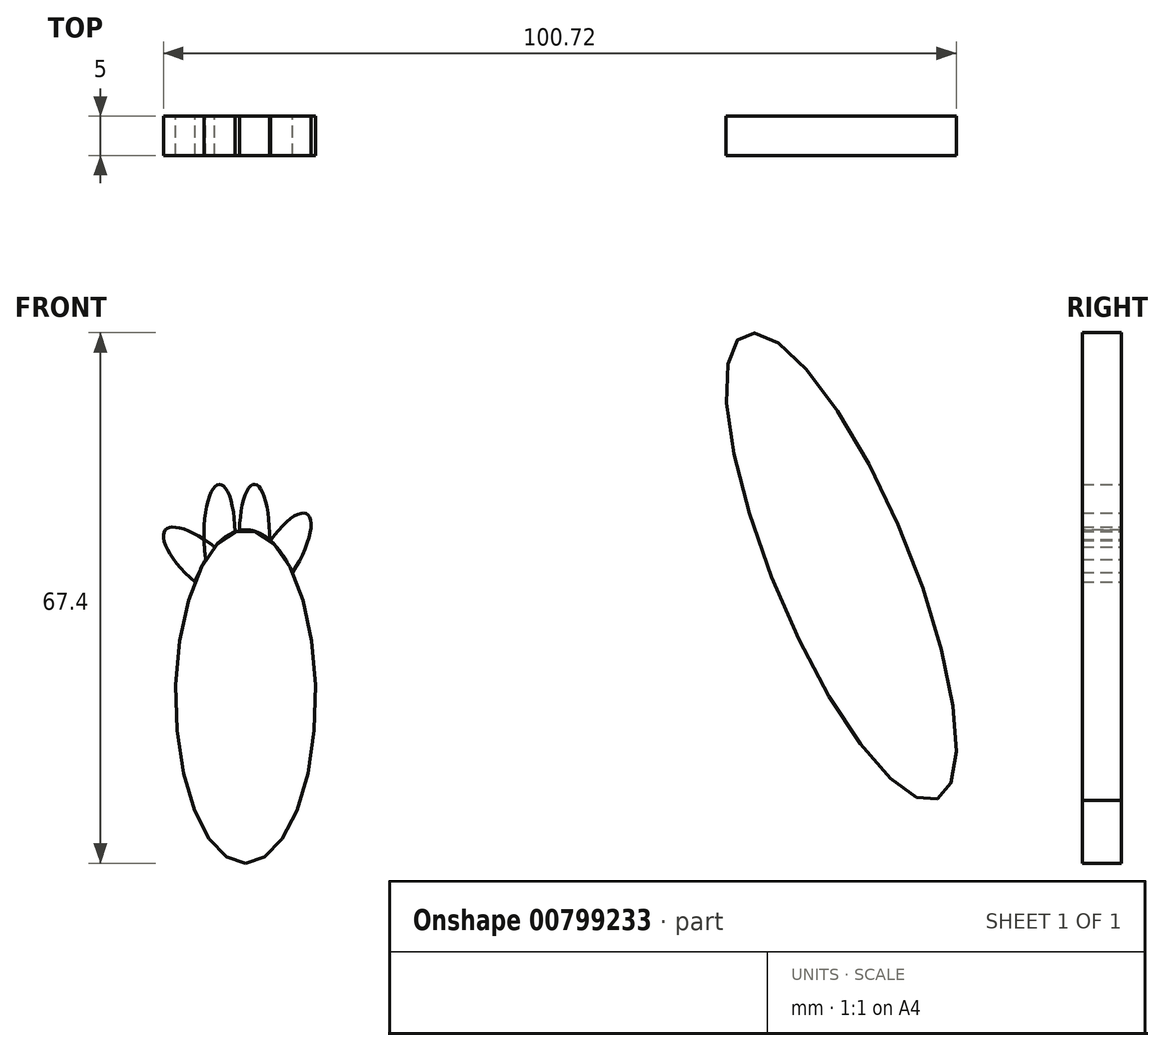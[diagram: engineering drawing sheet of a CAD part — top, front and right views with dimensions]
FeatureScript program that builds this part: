
annotation { "Feature Type Name" : "Feature", "Feature Type Description" : "" }
export const myFeature = defineFeature(function(context is Context, id is Id, definition is map)
    precondition{}
    {
        {
            var Q0;
            Q0=qCreatedBy(makeId("Front.planeOp"),FACE);
            var sketch = newSketch(context, id + "F0", { "sketchPlane" : qUnion([Q0])});
            skEllipse(sketch, "E0", {"center": v(-51.24, 0) * mm, "majorRadius": 21.18 * mm, "minorRadius": 8.9 * mm, "majorAxis": v(0, -1)});
            skSolve(sketch);
        }
        {
            var Q0;
            Q0=qCreatedBy(makeId("Front.planeOp"),FACE);
            var sketch = newSketch(context, id + "F1", { "sketchPlane" : qUnion([Q0])});
            skEllipse(sketch, "E1", {"center": v(24.4, 16.53) * mm, "majorRadius": 31.93 * mm, "minorRadius": 8.71 * mm, "majorAxis": v(0.38, -0.92)});
            skSolve(sketch);
        }
        {
            var Q0;
            Q0=makeQuery(id+"F0.imprint","IMPRINT",FACE,{"disambiguationData":[TD([[makeQuery(id+"F0.imprint","IMPRINT",EDGE,{"derivedFrom":sQuery(id+"F0.wireOp",EDGE,"E0")}),1.0]])]});
            var sketch = newSketch(context, id + "F2", { "sketchPlane" : qUnion([Q0])});
            skEllipse(sketch, "E2", {"center": v(-54.57, 20.52) * mm, "majorRadius": 6.43 * mm, "minorRadius": 1.98 * mm, "majorAxis": v(0, -1)});
            skEllipse(sketch, "E3", {"center": v(-50.13, 20.52) * mm, "majorRadius": 6.43 * mm, "minorRadius": 1.92 * mm, "majorAxis": v(0, -1)});
            skEllipse(sketch, "E4", {"center": v(-46.8, 17.64) * mm, "majorRadius": 6.47 * mm, "minorRadius": 2.27 * mm, "majorAxis": v(-0.51, -0.86)});
            skEllipse(sketch, "E5", {"center": v(-56.12, 16.51) * mm, "majorRadius": 7.07 * mm, "minorRadius": 2.5 * mm, "majorAxis": v(0.75, -0.66)});
            skSolve(sketch);
        }
        {
            var Q0;
            Q0=makeQuery(id+"F1.imprint","IMPRINT",FACE,{"disambiguationData":[TD([[makeQuery(id+"F1.imprint","IMPRINT",EDGE,{"derivedFrom":sQuery(id+"F1.wireOp",EDGE,"E1")}),1.0]])]});
            var Q1;
            Q1=makeQuery(id+"F0.imprint","IMPRINT",FACE,{"disambiguationData":[TD([[makeQuery(id+"F0.imprint","IMPRINT",EDGE,{"derivedFrom":sQuery(id+"F0.wireOp",EDGE,"E0")}),1.0]])]});
            var Q2;
            {var subQ0=sQuery(id+"F2.wireOp",EDGE,"E5");var subQ1=sQuery(id+"F2.wireOp",EDGE,"E2");var subQ2=makeQuery(id+"F2.imprint","INTERSECT",VERTEX,{"disambiguationData":[OD(0.0)],"derivedFrom":[subQ1,subQ0]});Q2=makeQuery(id+"F2.imprint","IMPRINT",FACE,{"disambiguationData":[TD([[makeQuery(id+"F2.imprint","IMPRINT",EDGE,{"disambiguationData":[TD([[subQ2,-1.0]])],"derivedFrom":subQ1}),-1.0]])]});}
            var Q3;
            {var subQ0=sQuery(id+"F2.wireOp",EDGE,"E5");var subQ1=sQuery(id+"F2.wireOp",EDGE,"E2");var subQ2=makeQuery(id+"F2.imprint","INTERSECT",VERTEX,{"disambiguationData":[OD(0.0)],"derivedFrom":[subQ1,subQ0]});Q3=makeQuery(id+"F2.imprint","IMPRINT",FACE,{"disambiguationData":[TD([[makeQuery(id+"F2.imprint","IMPRINT",EDGE,{"disambiguationData":[TD([[subQ2,1.0]])],"derivedFrom":subQ1}),1.0]])]});}
            var Q4;
            {var subQ0=sQuery(id+"F2.wireOp",EDGE,"E3");var subQ1=makeQuery(id+"F0.imprint","IMPRINT",EDGE,{"derivedFrom":sQuery(id+"F0.wireOp",EDGE,"E0")});var subQ2=makeQuery(id+"F2.imprint","INTERSECT",VERTEX,{"disambiguationData":[OD(0.0)],"derivedFrom":[subQ1,subQ0]});Q4=makeQuery(id+"F2.imprint","IMPRINT",FACE,{"disambiguationData":[TD([[makeQuery(id+"F2.imprint","IMPRINT",EDGE,{"disambiguationData":[TD([[subQ2,-1.0]])],"derivedFrom":subQ0}),1.0]])]});}
            var Q5;
            {var subQ0=sQuery(id+"F2.wireOp",EDGE,"E4");var subQ1=makeQuery(id+"F0.imprint","IMPRINT",EDGE,{"derivedFrom":sQuery(id+"F0.wireOp",EDGE,"E0")});var subQ2=makeQuery(id+"F2.imprint","INTERSECT",VERTEX,{"disambiguationData":[OD(0.0)],"derivedFrom":[subQ1,subQ0]});Q5=makeQuery(id+"F2.imprint","IMPRINT",FACE,{"disambiguationData":[TD([[makeQuery(id+"F2.imprint","IMPRINT",EDGE,{"disambiguationData":[TD([[subQ2,1.0]])],"derivedFrom":subQ0}),1.0]])]});}
            extrude(context, id + "F3", {"entities" : qUnion([Q0, Q1, Q2, Q3, Q4, Q5]), "depth" : 5 * mm, "offsetDistance" : 25 * mm});
        }
    });
